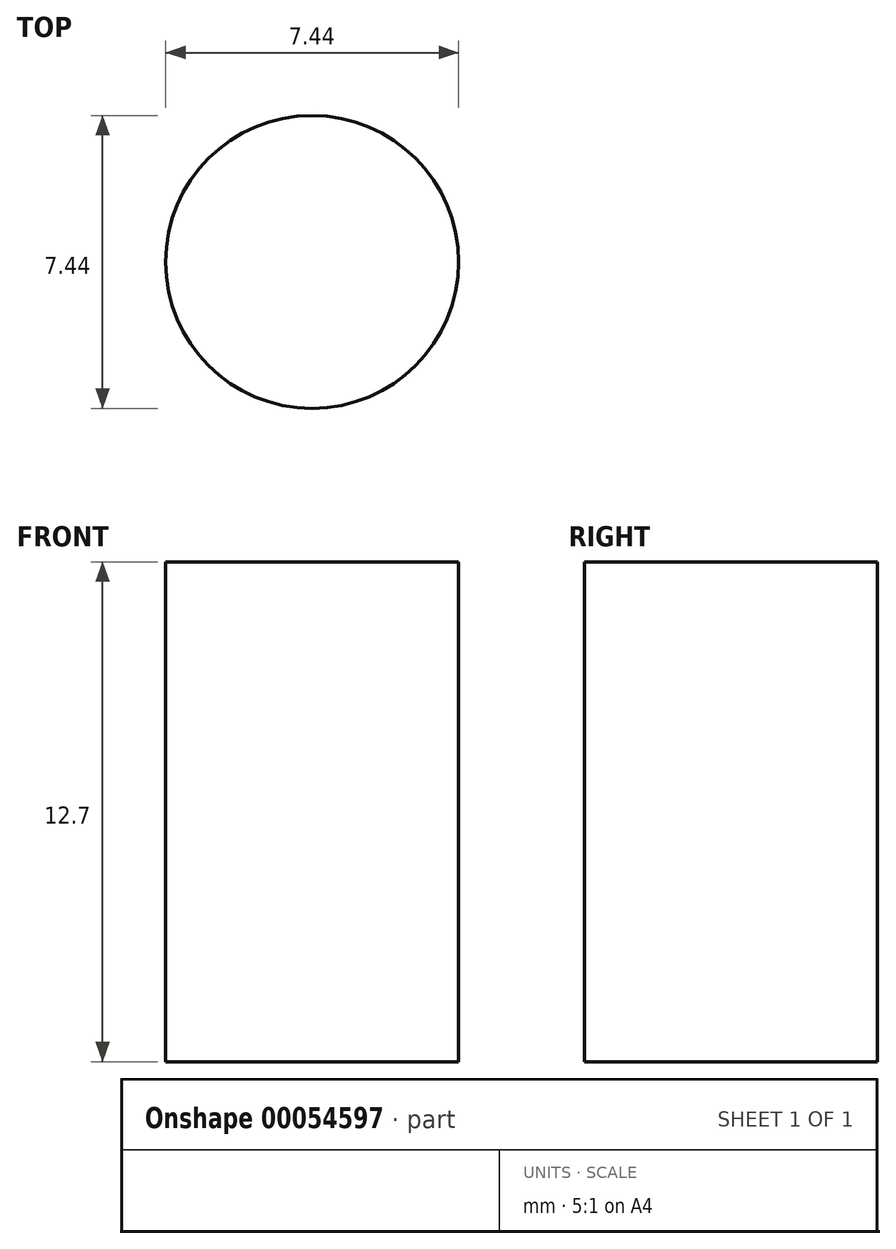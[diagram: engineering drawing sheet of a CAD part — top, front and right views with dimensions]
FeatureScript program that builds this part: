
annotation { "Feature Type Name" : "Feature", "Feature Type Description" : "" }
export const myFeature = defineFeature(function(context is Context, id is Id, definition is map)
    precondition{}
    {
        {
            var Q0;
            Q0=qCreatedBy(makeId("Top.planeOp"),FACE);
            var sketch = newSketch(context, id + "F0", { "sketchPlane" : qUnion([Q0])});
            skCircle(sketch, "E0", {"center": v(0, 0) * mm, "radius": 3.72 * mm});
            skSolve(sketch);
        }
        {
            var Q0;
            Q0=qSketchRegion(id+"F0",true);
            extrude(context, id + "F1", {"entities" : qUnion([Q0]), "depth" : 12.7 * mm});
        }
    });
